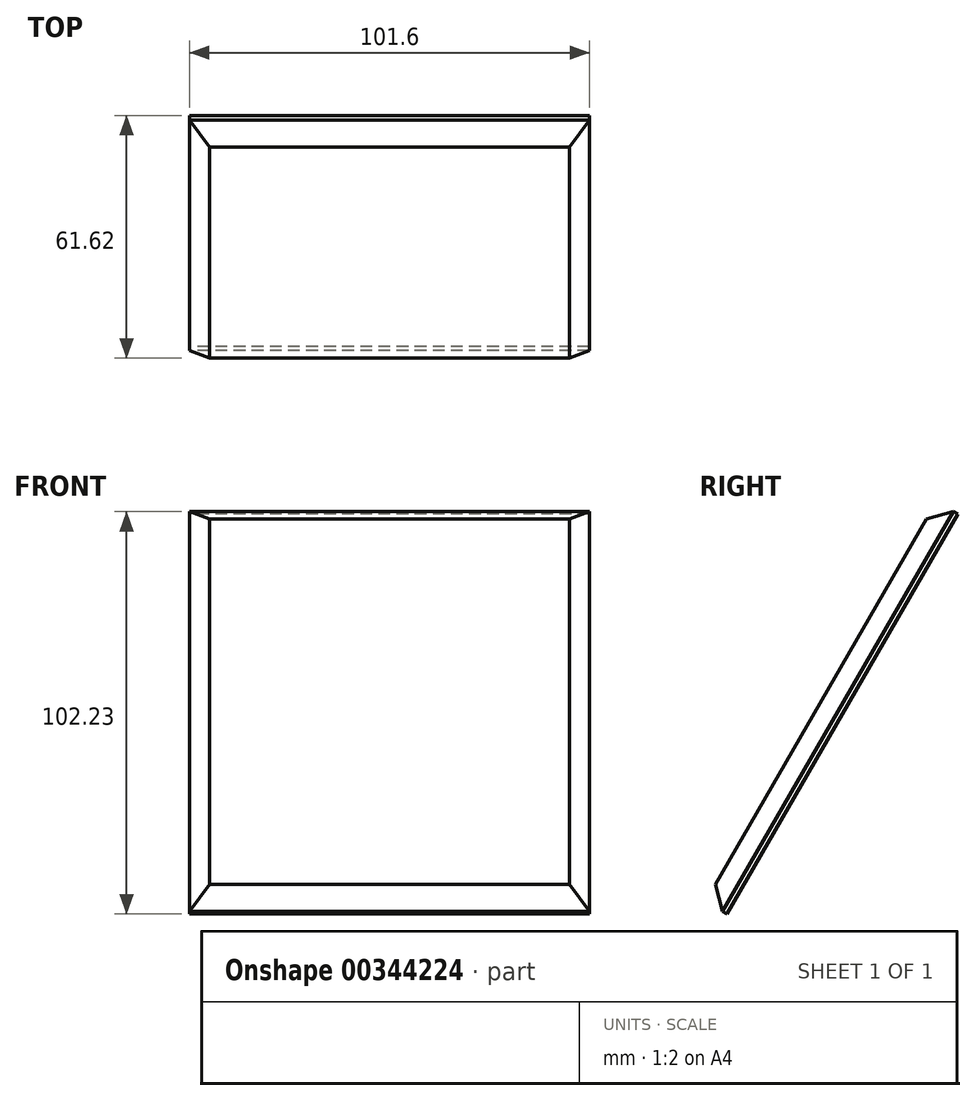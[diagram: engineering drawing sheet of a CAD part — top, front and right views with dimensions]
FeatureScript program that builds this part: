
annotation { "Feature Type Name" : "Feature", "Feature Type Description" : "" }
export const myFeature = defineFeature(function(context is Context, id is Id, definition is map)
    precondition{}
    {
        {
            var Q0;
            Q0=qCreatedBy(makeId("Right.planeOp"),FACE);
            var sketch = newSketch(context, id + "F0", { "sketchPlane" : qUnion([Q0])});
            skLineSegment(sketch, "E0", {"start": v(0, 101.6) * mm, "end": v(-58.66, 0) * mm});
            skLineSegment(sketch, "E1", {"start": v(5.5, 98.43) * mm, "end": v(-53.16, -3.18) * mm});
            skLineSegment(sketch, "E2", {"start": v(-53.16, -3.18) * mm, "end": v(-58.66, 0) * mm});
            skLineSegment(sketch, "E3", {"start": v(0, 101.6) * mm, "end": v(5.5, 98.43) * mm});
            skSolve(sketch);
        }
        {
            var Q0;
            Q0 = qSketchRegion(id + "F0", true);
            extrude(context, id + "F1", {"entities" : qUnion([Q0]), "depth" : 101.6 * mm});
        }
        {
            var Q0;
            Q0=makeQuery(id+"F1.opExtrude","SWEPT_FACE",FACE,{"disambiguationData":[OSD([sQuery(id+"F0.wireOp",EDGE,"E0")])]});
            chamfer(context, id + "F2", {"entities" : qUnion([Q0]), "width" : 5.08 * mm, "tangentPropagation" : true});
        }
    });
